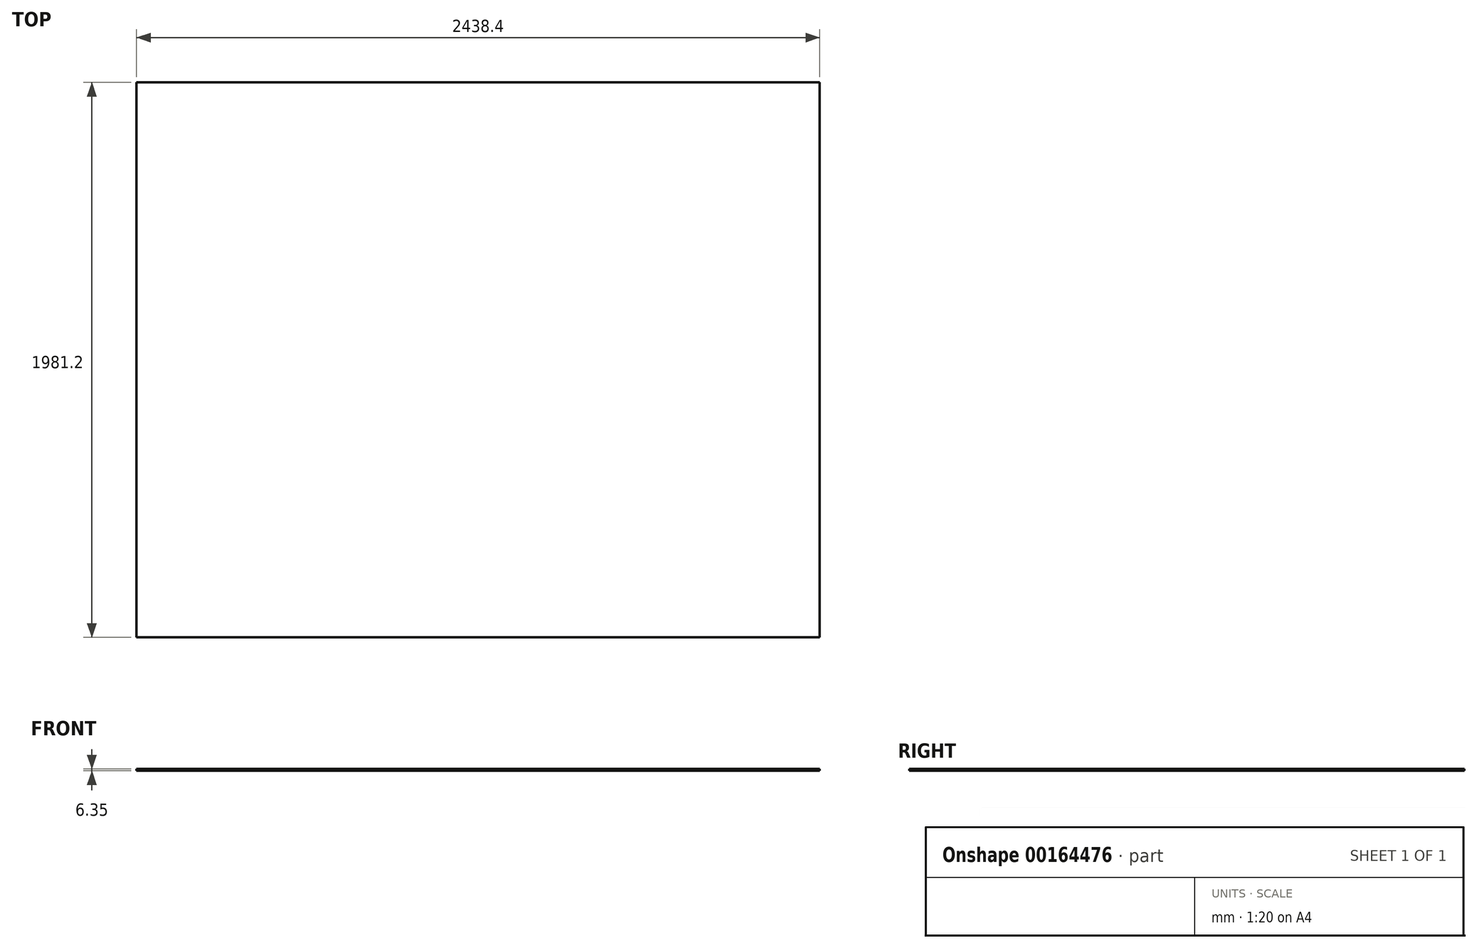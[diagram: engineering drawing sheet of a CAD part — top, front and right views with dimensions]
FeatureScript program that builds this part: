
annotation { "Feature Type Name" : "Feature", "Feature Type Description" : "" }
export const myFeature = defineFeature(function(context is Context, id is Id, definition is map)
    precondition{}
    {
        {
            var Q0;
            Q0=qCreatedBy(makeId("Top.planeOp"),FACE);
            var sketch = newSketch(context, id + "F0", { "sketchPlane" : qUnion([Q0])});
            skLineSegment(sketch, "E0.bottom", {"start": v(-1219.2, 990.6) * mm, "end": v(1219.2, 990.6) * mm});
            skLineSegment(sketch, "E0.top", {"start": v(-1219.2, -990.6) * mm, "end": v(1219.2, -990.6) * mm});
            skLineSegment(sketch, "E0.left", {"start": v(-1219.2, 990.6) * mm, "end": v(-1219.2, -990.6) * mm});
            skLineSegment(sketch, "E0.right", {"start": v(1219.2, 990.6) * mm, "end": v(1219.2, -990.6) * mm});
            skPoint(sketch, "E1", {"position": v(0, 990.6) * mm});
            skPoint(sketch, "E2", {"position": v(-1219.2, 0) * mm});
            skLineSegment(sketch, "E3", {"start": v(-1219.2, 0) * mm, "end": v(0, 0) * mm, "construction": true});
            skLineSegment(sketch, "E4", {"start": v(0, 0) * mm, "end": v(0, 990.6) * mm, "construction": true});
            skSolve(sketch);
        }
        {
            var Q0;
            Q0=makeQuery(id+"F0.imprint","IMPRINT",FACE,{"disambiguationData":[TD([[makeQuery(id+"F0.imprint","IMPRINT",EDGE,{"derivedFrom":sQuery(id+"F0.wireOp",EDGE,"E0.bottom")}),-1.0]])]});
            extrude(context, id + "F1", {"entities" : qUnion([Q0]), "oppositeDirection" : true, "depth" : 6.35 * mm});
        }
    });
